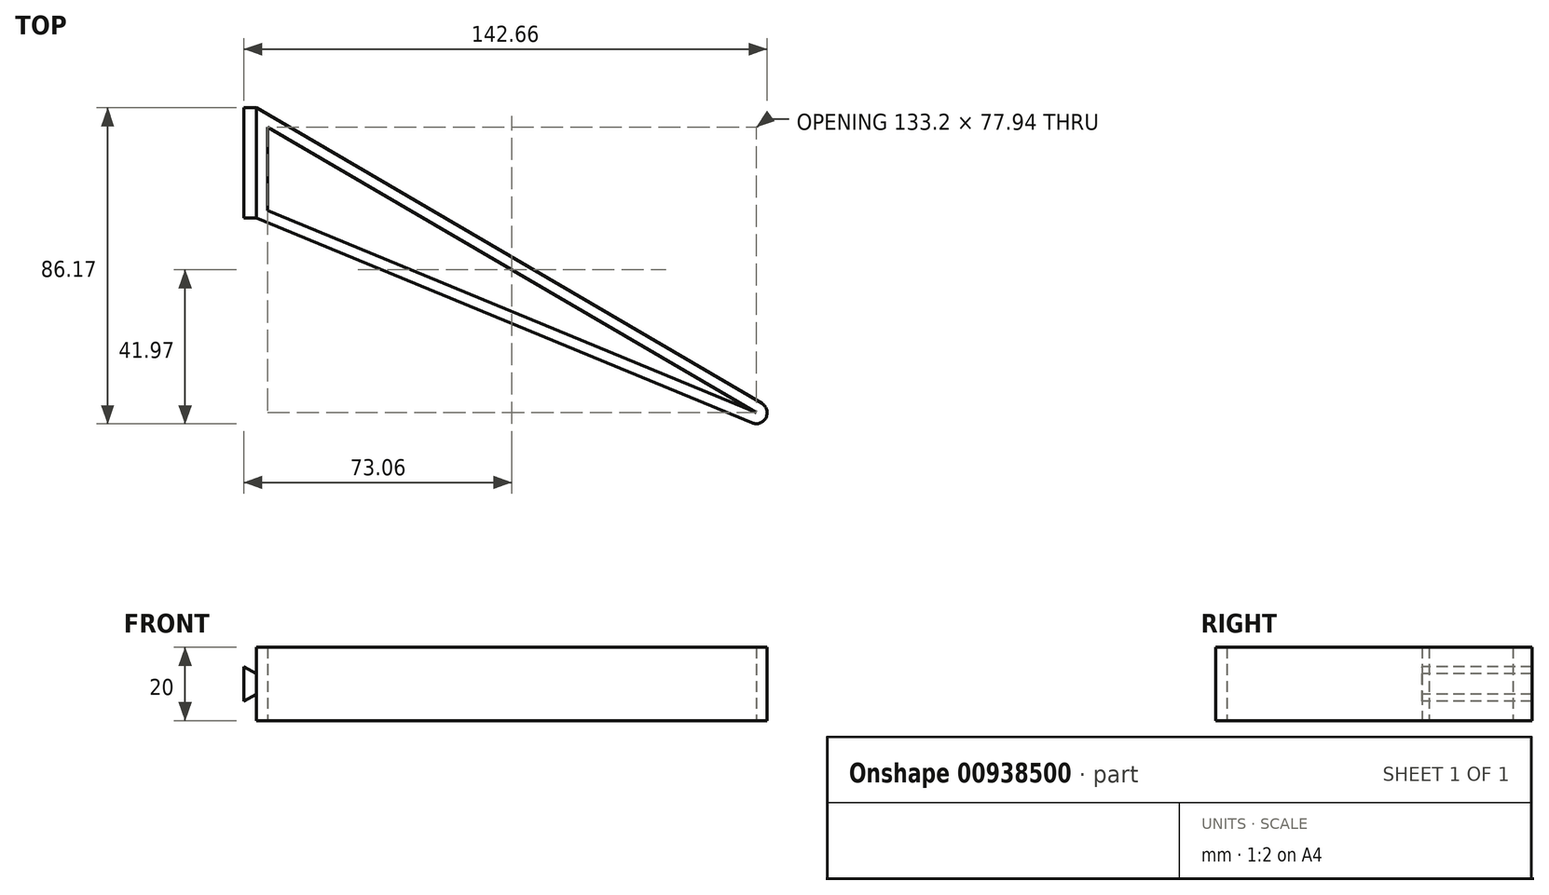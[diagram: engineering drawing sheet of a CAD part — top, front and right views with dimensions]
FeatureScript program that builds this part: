
annotation { "Feature Type Name" : "Feature", "Feature Type Description" : "" }
export const myFeature = defineFeature(function(context is Context, id is Id, definition is map)
    precondition{}
    {
        {
            var Q0;
            Q0=qCreatedBy(makeId("Top.planeOp"),FACE);
            var sketch = newSketch(context, id + "F0", { "sketchPlane" : qUnion([Q0])});
            skLineSegment(sketch, "E0", {"start": v(0, 0) * mm, "end": v(0, 30) * mm});
            skLineSegment(sketch, "E1", {"start": v(0, 0) * mm, "end": v(135.05, -55.94) * mm});
            skLineSegment(sketch, "E2", {"start": v(0, 30) * mm, "end": v(137.71, -50.58) * mm});
            skArc(sketch, "E3", {"start": v(135.05, -55.94) * mm, "mid": v(138.89, -54.5) * mm, "end": v(137.71, -50.58) * mm});
            skPoint(sketch, "E4.orphan", {"position": v(175.54, -72.7) * mm});
            skLineSegment(sketch, "E5.0", {"start": v(3, 24.77) * mm, "end": v(136.2, -53.17) * mm});
            skLineSegment(sketch, "E5.1", {"start": v(3, 2) * mm, "end": v(3, 24.77) * mm});
            skLineSegment(sketch, "E5.2", {"start": v(3, 2) * mm, "end": v(136.2, -53.17) * mm});
            skSolve(sketch);
        }
        {
            var Q0;
            Q0 = qSketchRegion(id + "F0", true);
            extrude(context, id + "F1", {"entities" : qUnion([Q0]), "depth" : 20 * mm, "offsetDistance" : 25 * mm});
        }
        {
            var Q0;
            Q0=qCreatedBy(makeId("Front.planeOp"),FACE);
            var sketch = newSketch(context, id + "F2", { "sketchPlane" : qUnion([Q0])});
            skLineSegment(sketch, "E6", {"start": v(0, 12.75) * mm, "end": v(0, 7.25) * mm});
            skLineSegment(sketch, "E7", {"start": v(0, 7.25) * mm, "end": v(-3.46, 5.25) * mm});
            skLineSegment(sketch, "E8", {"start": v(-3.46, 5.25) * mm, "end": v(-3.46, 14.75) * mm});
            skLineSegment(sketch, "E9", {"start": v(-3.46, 14.75) * mm, "end": v(0, 12.75) * mm});
            skSolve(sketch);
        }
        {
            var Q0;
            Q0=makeQuery(id+"F2.imprint","IMPRINT",FACE,{"disambiguationData":[TD([[makeQuery(id+"F2.imprint","IMPRINT",EDGE,{"derivedFrom":sQuery(id+"F2.wireOp",EDGE,"E6")}),-1.0]])]});
            extrude(context, id + "F3", {"entities" : qUnion([Q0]), "operationType" : NewBodyOperationType.ADD, "oppositeDirection" : true, "depth" : 30 * mm, "offsetDistance" : 25 * mm});
        }
    });
